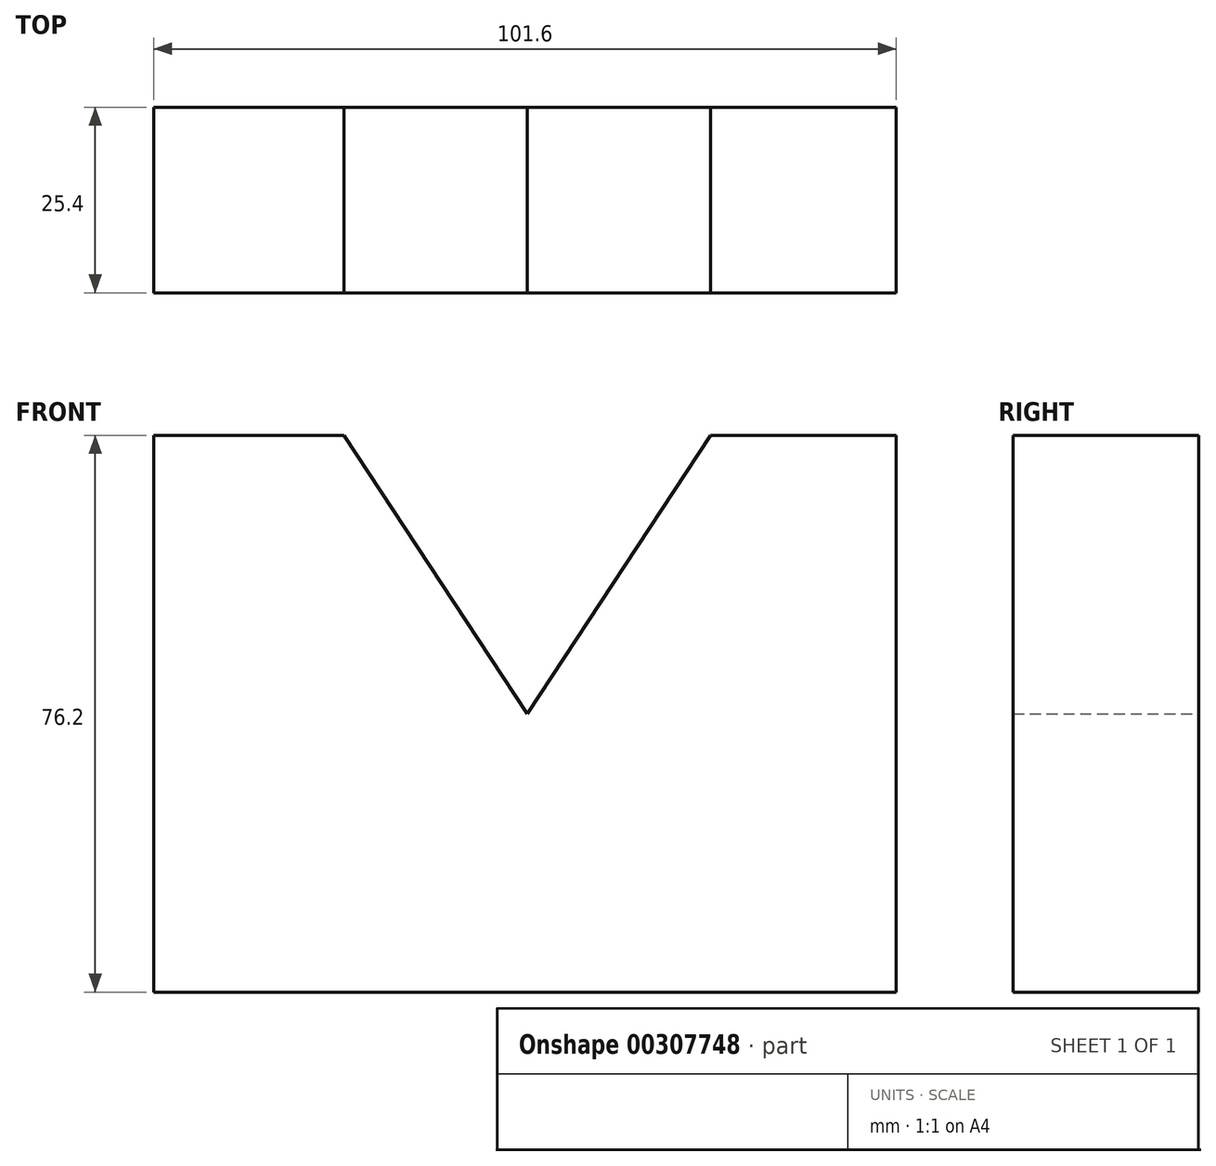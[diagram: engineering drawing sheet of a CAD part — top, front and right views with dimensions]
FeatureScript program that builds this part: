
annotation { "Feature Type Name" : "Feature", "Feature Type Description" : "" }
export const myFeature = defineFeature(function(context is Context, id is Id, definition is map)
    precondition{}
    {
        {
            var Q0;
            Q0=qCreatedBy(makeId("Front.planeOp"),FACE);
            var sketch = newSketch(context, id + "F0", { "sketchPlane" : qUnion([Q0])});
            skLineSegment(sketch, "E0", {"start": v(-64.75, -62.09) * mm, "end": v(36.85, -62.09) * mm});
            skLineSegment(sketch, "E1", {"start": v(36.85, -62.09) * mm, "end": v(36.85, 14.11) * mm});
            skLineSegment(sketch, "E2", {"start": v(-64.75, -62.09) * mm, "end": v(-64.75, 14.11) * mm});
            skLineSegment(sketch, "E3", {"start": v(-64.75, 14.11) * mm, "end": v(-38.69, 14.11) * mm});
            skLineSegment(sketch, "E4", {"start": v(-38.69, 14.11) * mm, "end": v(-13.66, -23.99) * mm});
            skLineSegment(sketch, "E5", {"start": v(36.85, 14.11) * mm, "end": v(11.45, 14.11) * mm});
            skLineSegment(sketch, "E6", {"start": v(11.45, 14.11) * mm, "end": v(-13.66, -23.99) * mm});
            skSolve(sketch);
        }
        {
            var Q0;
            Q0=makeQuery(id+"F0.imprint","IMPRINT",FACE,{"disambiguationData":[TD([[makeQuery(id+"F0.imprint","IMPRINT",EDGE,{"derivedFrom":sQuery(id+"F0.wireOp",EDGE,"E0")}),1.0]])]});
            extrude(context, id + "F1", {"entities" : qUnion([Q0]), "depth" : 25.4 * mm});
        }
    });
